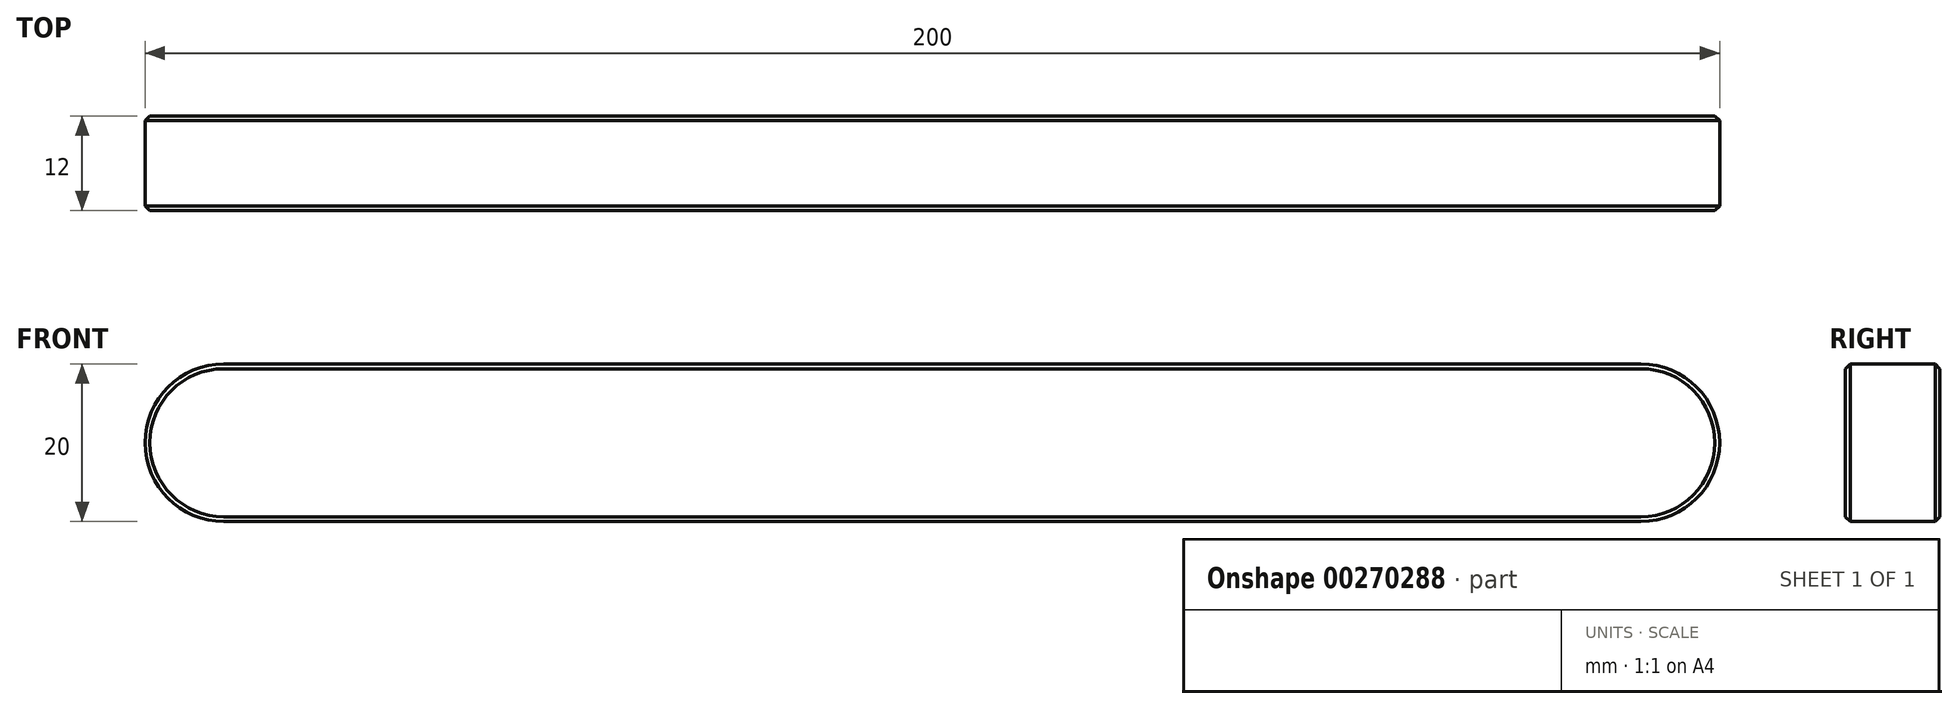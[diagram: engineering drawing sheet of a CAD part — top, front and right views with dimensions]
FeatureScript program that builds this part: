
annotation { "Feature Type Name" : "Feature", "Feature Type Description" : "" }
export const myFeature = defineFeature(function(context is Context, id is Id, definition is map)
    precondition{}
    {
        {
            var Q0;
            Q0=qCreatedBy(makeId("Front.planeOp"),FACE);
            var sketch = newSketch(context, id + "F0", { "sketchPlane" : qUnion([Q0])});
            skLineSegment(sketch, "E0.bottom", {"start": v(100, 10) * mm, "end": v(-100, 10) * mm});
            skLineSegment(sketch, "E0.top", {"start": v(100, -10) * mm, "end": v(-100, -10) * mm});
            skLineSegment(sketch, "E0.left", {"start": v(100, 10) * mm, "end": v(100, -10) * mm});
            skLineSegment(sketch, "E0.right", {"start": v(-100, 10) * mm, "end": v(-100, -10) * mm});
            skPoint(sketch, "E0.middle", {"position": v(0, 0) * mm});
            skSolve(sketch);
        }
        {
            var Q0;
            Q0=makeQuery(id+"F0.imprint","IMPRINT",FACE,{"disambiguationData":[TD([[makeQuery(id+"F0.imprint","IMPRINT",EDGE,{"derivedFrom":sQuery(id+"F0.wireOp",EDGE,"E0.bottom")}),1.0]])]});
            extrude(context, id + "F1", {"entities" : qUnion([Q0]), "endBound" : BoundingType.SYMMETRIC, "depth" : 12 * mm});
        }
        {
            var Q0;
            Q0=makeQuery(id+"F1.opExtrude","SWEPT_EDGE",EDGE,{"disambiguationData":[OSD([sQuery(id+"F0.wireOp",EDGE,"E0.top"),sQuery(id+"F0.wireOp",EDGE,"E0.left")])]});
            var Q1;
            Q1=makeQuery(id+"F1.opExtrude","SWEPT_EDGE",EDGE,{"disambiguationData":[OSD([sQuery(id+"F0.wireOp",EDGE,"E0.bottom"),sQuery(id+"F0.wireOp",EDGE,"E0.left")])]});
            var Q2;
            Q2=makeQuery(id+"F1.opExtrude","SWEPT_EDGE",EDGE,{"disambiguationData":[OSD([sQuery(id+"F0.wireOp",EDGE,"E0.top"),sQuery(id+"F0.wireOp",EDGE,"E0.right")])]});
            var Q3;
            Q3=makeQuery(id+"F1.opExtrude","SWEPT_EDGE",EDGE,{"disambiguationData":[OSD([sQuery(id+"F0.wireOp",EDGE,"E0.bottom"),sQuery(id+"F0.wireOp",EDGE,"E0.right")])]});
            fillet(context, id + "F2", {"entities" : qUnion([Q0, Q1, Q2, Q3]), "radius" : 10 * mm, "tangentPropagation" : true, "allowEdgeOverflow" : false});
        }
        {
            var Q0;
            Q0=makeQuery(id+"F1.opExtrude","CAP_EDGE",EDGE,{"disambiguationData":[OSD([sQuery(id+"F0.wireOp",EDGE,"E0.bottom")])],"isStart":false});
            var Q1;
            Q1=makeQuery(id+"F1.opExtrude","CAP_FACE",FACE,{"disambiguationData":[OSD([sQuery(id+"F0.wireOp",EDGE,"E0.bottom"),sQuery(id+"F0.wireOp",EDGE,"E0.top"),sQuery(id+"F0.wireOp",EDGE,"E0.left"),sQuery(id+"F0.wireOp",EDGE,"E0.right")])],"isStart":false});
            var Q2;
            Q2=makeQuery(id+"F1.opExtrude","CAP_FACE",FACE,{"disambiguationData":[OSD([sQuery(id+"F0.wireOp",EDGE,"E0.bottom"),sQuery(id+"F0.wireOp",EDGE,"E0.top"),sQuery(id+"F0.wireOp",EDGE,"E0.left"),sQuery(id+"F0.wireOp",EDGE,"E0.right")])],"isStart":true});
            chamfer(context, id + "F3", {"entities" : qUnion([Q0, Q1, Q2]), "width" : .6 * mm, "tangentPropagation" : true});
        }
    });
